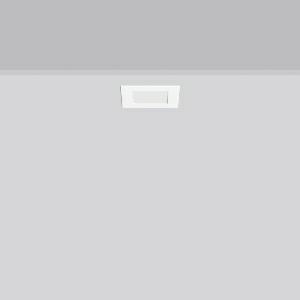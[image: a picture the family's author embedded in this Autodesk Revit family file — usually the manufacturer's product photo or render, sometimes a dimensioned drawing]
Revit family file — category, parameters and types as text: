
# Revit family: toledo_flat_square_e_901485_002_76_0f82
name_source: partatom
category: Lighting Fixtures
units: mm (PartAtom-declared; Revit-internal decimal feet)

## family parameters
Cut with Voids When Loaded = No
Host = Face
Light Source = No
Part Type = Normal
Room Calculation Point = No
Round Connector Dimension = Use Diameter
Shared = No

## types (1)
- TOLEDO FLAT square E (1 x LED Modul 830, 420 lm, 3000)
    Apparent Load = 5 VA
    CIE Flux Codes = 49 80 96 100 100
    Color Rendering = 80
    Color Temperature = 3000
    Default Elevation = 1800 mm
    Description = Series: TOLEDO FLAT square
Ultra thin recessed downlight. Housing: die-cast aluminium. Light guide and diffuser made of non-yellowing PMMA, opal matt. Ceiling installation with spring system. Mounting depth depends on ceiling strength. Suitable for through-wiring with separately available accessories. Surface mounted housing as accessory for all sizes. Retrofittable decorative cylinders made of chintz fabric as accessory, optional with satin finish plastic diffuser. Through-wiring box (5 pole) available as accessory. 
Colour: white
Length: 110 mm
Width: 110 mm
Height: 3 mm
Cut-out length: 96 mm
Cut-out width: 96 mm
Recess height: 31-56 mm
Luminaire: recess height: 31-51 mm
Lamp: LED
Socket: without socket
Colour temperature: 3000K
Colour rendering index (CRI): 80
System power: 5 W
Rated luminous flux: 420 lm
Luminous efficiency: 84 lm/W
Control gear: Converter, dimmable, DALI
Protection class: II
Type of protection: IP 54
    Height = 0 mm  [stored 0 ft]
    Lamp = 1 x LED Modul 830
    Lamp Light Flux = 420 lm
    Lamp count = 1
    Length = 110 mm
    Lifetime = 50000 h
    Luminous efficacy = 84 lm/W
    Manufacturer = RZB
    ModVariant = No
    Model = 901485.002.76
    Mounting Place = Ceiling
    Mounting Type = Recessed
    Number of Poles = 1
    OnlyDefault = Yes
    Power Factor = 1
    Product Name = TOLEDO FLAT square E
    Product group = Recessed downlights
    ProductGroupID = 402
    Protection Class = Protection class II
    Protection Degree = IP 20
    RLX_Detail_Level = 1
    RLX_Emergency_Light_Flux = 0 lm
    RLX_Emergency_Type = 0
    RLX_Emergency_Type_DB = No
    RlxData = <blob elided: 57621 chars, md5=7183db99>
    Socket = socket
    Standby Power = 0 W
    System Light Flux = 420 lm
    System Power = 5 W
    Type Comments = Product without accessories
    Type Image = 901485.002.jpg
    URL = http://relux.com
    VarID = ---
    Voltage = 230 V
    Voltage Range = 220-240 V
    Weight = 0.00 kg
    Width = 110 mm

note: [stored X ft] marks values corroborated as IEEE doubles in the binary element streams (Revit-internal decimal feet)

## geometry (parser evidence)
native form markers: Blend x4, Sweep x9
no freeform markers — native parametric forms only
